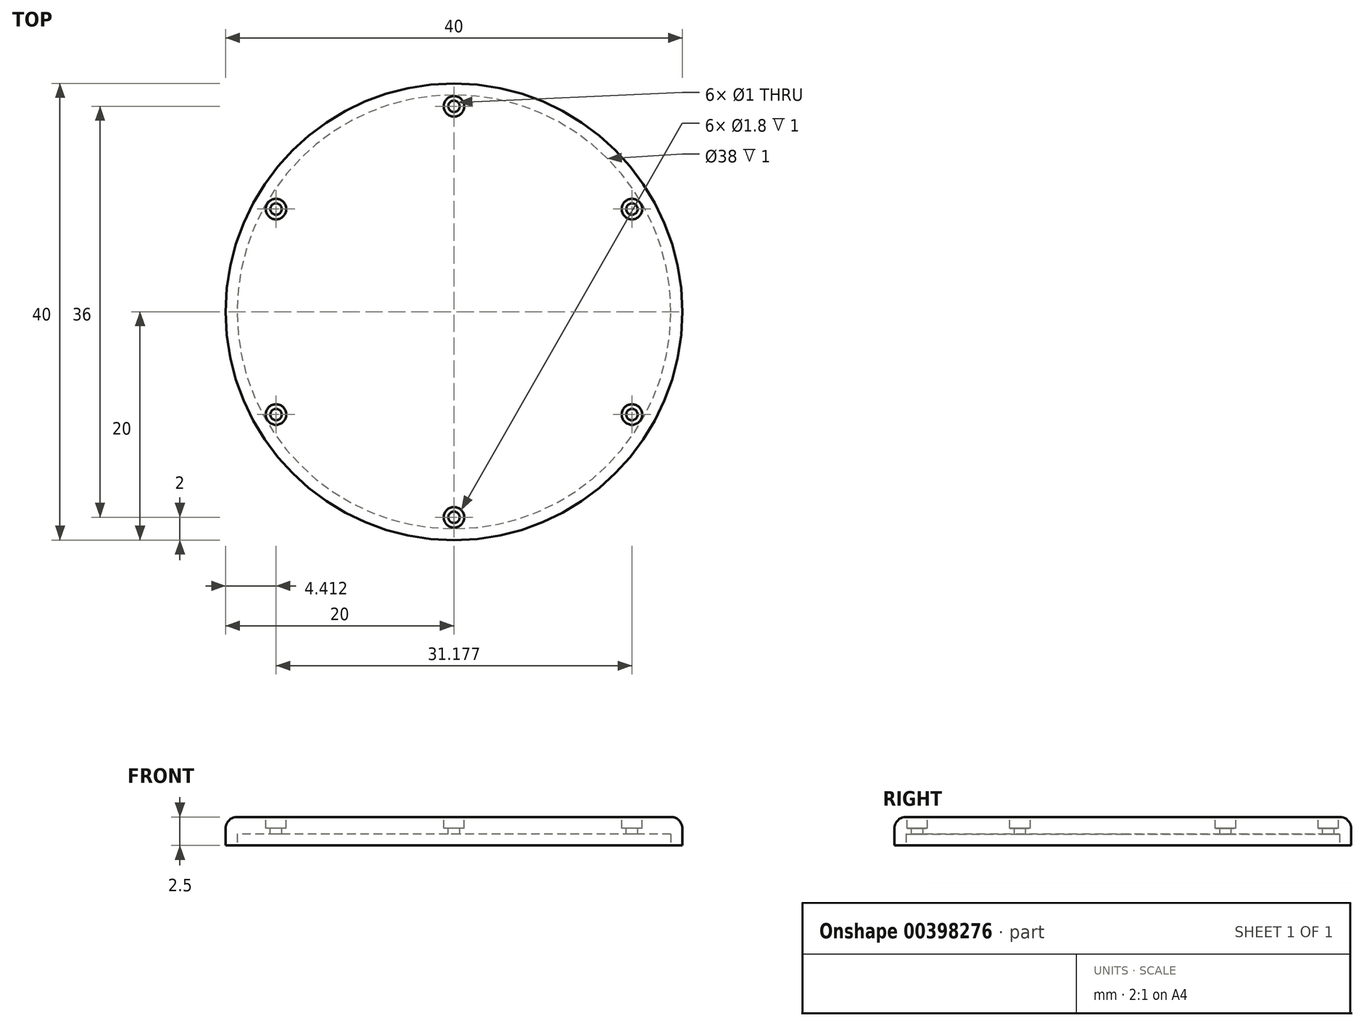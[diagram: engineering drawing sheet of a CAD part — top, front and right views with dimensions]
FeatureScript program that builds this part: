
annotation { "Feature Type Name" : "Feature", "Feature Type Description" : "" }
export const myFeature = defineFeature(function(context is Context, id is Id, definition is map)
    precondition{}
    {
        {
            var Q0;
            Q0=qCreatedBy(makeId("Top.planeOp"),FACE);
            var sketch = newSketch(context, id + "F0", { "sketchPlane" : qUnion([Q0])});
            skCircle(sketch, "E0", {"center": v(0, 0) * mm, "radius": 20 * mm});
            skCircle(sketch, "E1", {"center": v(0, 0) * mm, "radius": 19 * mm});
            skSolve(sketch);
        }
        {
            var Q0;
            Q0=makeQuery(id+"F0.imprint","IMPRINT",FACE,{"disambiguationData":[TD([[makeQuery(id+"F0.imprint","IMPRINT",EDGE,{"derivedFrom":sQuery(id+"F0.wireOp",EDGE,"E0")}),1.0]])]});
            extrude(context, id + "F1", {"entities" : qUnion([Q0]), "depth" : 1 * mm});
        }
        {
            var Q0;
            Q0=makeQuery(id+"F1.opExtrude","CAP_FACE",FACE,{"disambiguationData":[OSD([sQuery(id+"F0.wireOp",EDGE,"E0"),sQuery(id+"F0.wireOp",EDGE,"E1")])],"isStart":false});
            var sketch = newSketch(context, id + "F2", { "sketchPlane" : qUnion([Q0])});
            skCircle(sketch, "E2.0", {"center": v(0, 0) * mm, "radius": 20 * mm});
            skSolve(sketch);
        }
        {
            var Q0;
            Q0 = qSketchRegion(id + "F2", true);
            extrude(context, id + "F3", {"entities" : qUnion([Q0]), "operationType" : NewBodyOperationType.ADD, "depth" : 1.5 * mm});
        }
        {
            var Q0;
            Q0=makeQuery(id+"F3.opExtrude","CAP_FACE",FACE,{"disambiguationData":[OSD([sQuery(id+"F2.wireOp",EDGE,"E2.0")])],"isStart":false});
            var sketch = newSketch(context, id + "F4", { "sketchPlane" : qUnion([Q0])});
            skCircle(sketch, "E3", {"center": v(0, 0) * mm, "radius": 18 * mm, "construction": true});
            skLineSegment(sketch, "E4", {"start": v(0, 0) * mm, "end": v(21.7, 12.53) * mm, "construction": true});
            skLineSegment(sketch, "E5", {"start": v(0, 0) * mm, "end": v(22.1, -12.75) * mm, "construction": true});
            skLineSegment(sketch, "E6", {"start": v(0, 0) * mm, "end": v(-22.66, 13.08) * mm, "construction": true});
            skLineSegment(sketch, "E7", {"start": v(0, 0) * mm, "end": v(-21.02, -12.13) * mm, "construction": true});
            skCircle(sketch, "E8", {"center": v(0, 18) * mm, "radius": 0.5 * mm});
            skCircle(sketch, "E9", {"center": v(15.59, 9) * mm, "radius": 0.5 * mm});
            skCircle(sketch, "E10", {"center": v(15.59, -9) * mm, "radius": 0.5 * mm});
            skCircle(sketch, "E11", {"center": v(0, -18) * mm, "radius": 0.5 * mm});
            skCircle(sketch, "E12", {"center": v(-15.59, -9) * mm, "radius": 0.5 * mm});
            skCircle(sketch, "E13", {"center": v(-15.59, 9) * mm, "radius": 0.5 * mm});
            skSolve(sketch);
        }
        {
            var Q0;
            Q0 = qSketchRegion(id + "F4", true);
            extrude(context, id + "F5", {"entities" : qUnion([Q0]), "operationType" : NewBodyOperationType.REMOVE, "endBound" : BoundingType.THROUGH_ALL, "oppositeDirection" : true, "depth" : 25 * mm});
        }
        {
            var Q0;
            Q0=makeQuery(id+"F3.opExtrude","CAP_FACE",FACE,{"disambiguationData":[OSD([sQuery(id+"F2.wireOp",EDGE,"E2.0")])],"isStart":false});
            var sketch = newSketch(context, id + "F6", { "sketchPlane" : qUnion([Q0])});
            skCircle(sketch, "E14.0", {"center": v(0, 18) * mm, "radius": 0.5 * mm, "construction": true});
            skCircle(sketch, "E15.0", {"center": v(-15.59, 9) * mm, "radius": 0.5 * mm, "construction": true});
            skCircle(sketch, "E16.0", {"center": v(-15.59, -9) * mm, "radius": 0.5 * mm, "construction": true});
            skCircle(sketch, "E17.0", {"center": v(0, -18) * mm, "radius": 0.5 * mm, "construction": true});
            skCircle(sketch, "E18.0", {"center": v(15.59, -9) * mm, "radius": 0.5 * mm, "construction": true});
            skCircle(sketch, "E19.0", {"center": v(15.59, 9) * mm, "radius": 0.5 * mm, "construction": true});
            skCircle(sketch, "E20", {"center": v(0, 18) * mm, "radius": 0.9 * mm});
            skCircle(sketch, "E21", {"center": v(-15.59, 9) * mm, "radius": 0.9 * mm});
            skCircle(sketch, "E22", {"center": v(-15.59, -9) * mm, "radius": 0.9 * mm});
            skCircle(sketch, "E23", {"center": v(0, -18) * mm, "radius": 0.9 * mm});
            skCircle(sketch, "E24", {"center": v(15.59, -9) * mm, "radius": 0.9 * mm});
            skCircle(sketch, "E25", {"center": v(15.59, 9) * mm, "radius": 0.9 * mm});
            skSolve(sketch);
        }
        {
            var Q0;
            Q0 = qSketchRegion(id + "F6", true);
            extrude(context, id + "F7", {"entities" : qUnion([Q0]), "operationType" : NewBodyOperationType.REMOVE, "oppositeDirection" : true, "depth" : 1 * mm});
        }
        {
            var Q0;
            Q0=qCreatedBy(makeId("Right.planeOp"),FACE);
            var sketch = newSketch(context, id + "F8", { "sketchPlane" : qUnion([Q0])});
            skLineSegment(sketch, "E26", {"start": v(20, 2.5) * mm, "end": v(20, 1.5) * mm});
            skLineSegment(sketch, "E27.0.0", {"start": v(19, 2.5) * mm, "end": v(20, 2.5) * mm});
            skArc(sketch, "E28", {"start": v(20, 1.5) * mm, "mid": v(19.7, 2.2) * mm, "end": v(19, 2.5) * mm});
            skPoint(sketch, "E29.orphan", {"position": v(-20, 2.5) * mm});
            skLineSegment(sketch, "E30", {"start": v(0, 0) * mm, "end": v(0, 7.7) * mm, "construction": true});
            skSolve(sketch);
        }
        {
            var Q0;
            Q0 = qSketchRegion(id + "F8", true);
            var Q1;
            Q1=sQuery(id+"F8.wireOp",EDGE,"E30");
            revolve(context, id + "F9", {"operationType" : NewBodyOperationType.REMOVE, "entities" : qUnion([Q0]), "axis" : qUnion([Q1]), "revolveType" : RevolveType.FULL, "oppositeDirection" : true});
        }
    });
